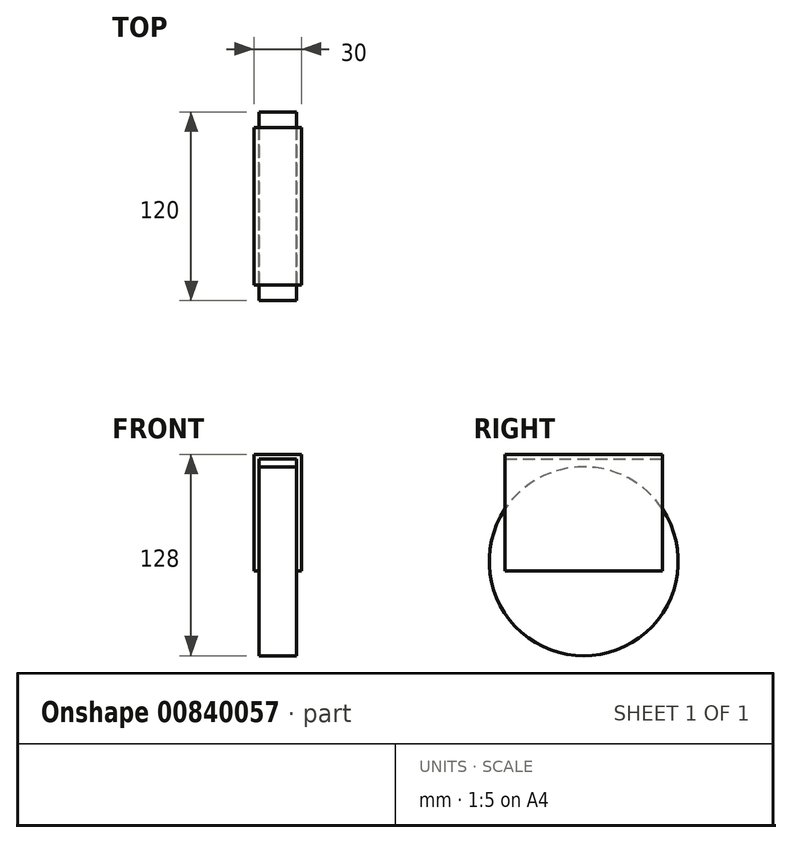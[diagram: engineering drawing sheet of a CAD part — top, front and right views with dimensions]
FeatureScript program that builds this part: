
annotation { "Feature Type Name" : "Feature", "Feature Type Description" : "" }
export const myFeature = defineFeature(function(context is Context, id is Id, definition is map)
    precondition{}
    {
        {
            var Q0;
            Q0=qCreatedBy(makeId("Front.planeOp"),FACE);
            var sketch = newSketch(context, id + "F0", { "sketchPlane" : qUnion([Q0])});
            skLineSegment(sketch, "E0", {"start": v(0, 65) * mm, "end": v(-12, 65) * mm});
            skLineSegment(sketch, "E1", {"start": v(-12, 65) * mm, "end": v(-12, -6) * mm});
            skLineSegment(sketch, "E2", {"start": v(-12, -6) * mm, "end": v(-15, -6) * mm});
            skLineSegment(sketch, "E3", {"start": v(-15, -6) * mm, "end": v(-15, 68) * mm});
            skLineSegment(sketch, "E4", {"start": v(-15, 68) * mm, "end": v(0, 68) * mm});
            skLineSegment(sketch, "E5.MirrorCS", {"start": v(15, 68) * mm, "end": v(0, 68) * mm});
            skLineSegment(sketch, "E6.MirrorCS", {"start": v(0, 65) * mm, "end": v(12, 65) * mm});
            skLineSegment(sketch, "E7.MirrorCS", {"start": v(15, -6) * mm, "end": v(15, 68) * mm});
            skLineSegment(sketch, "E8.MirrorCS", {"start": v(12, 65) * mm, "end": v(12, -6) * mm});
            skLineSegment(sketch, "E9.MirrorCS", {"start": v(12, -6) * mm, "end": v(15, -6) * mm});
            skSolve(sketch);
        }
        {
            var Q0;
            Q0=makeQuery(id+"F0.imprint","IMPRINT",FACE,{"disambiguationData":[TD([[makeQuery(id+"F0.imprint","IMPRINT",EDGE,{"derivedFrom":sQuery(id+"F0.wireOp",EDGE,"E0")}),-1.0]])]});
            extrude(context, id + "F1", {"entities" : qUnion([Q0]), "endBound" : BoundingType.SYMMETRIC, "depth" : 100 * mm, "offsetDistance" : 25 * mm});
        }
        {
            var Q0;
            Q0=qCreatedBy(makeId("Right.planeOp"),FACE);
            var sketch = newSketch(context, id + "F2", { "sketchPlane" : qUnion([Q0])});
            skCircle(sketch, "E10", {"center": v(0, 0) * mm, "radius": 60 * mm});
            skSolve(sketch);
        }
        {
            var Q0;
            Q0 = qSketchRegion(id + "F2", true);
            extrude(context, id + "F3", {"entities" : qUnion([Q0]), "operationType" : NewBodyOperationType.ADD, "endBound" : BoundingType.SYMMETRIC, "depth" : 24 * mm, "offsetDistance" : 25 * mm});
        }
    });
